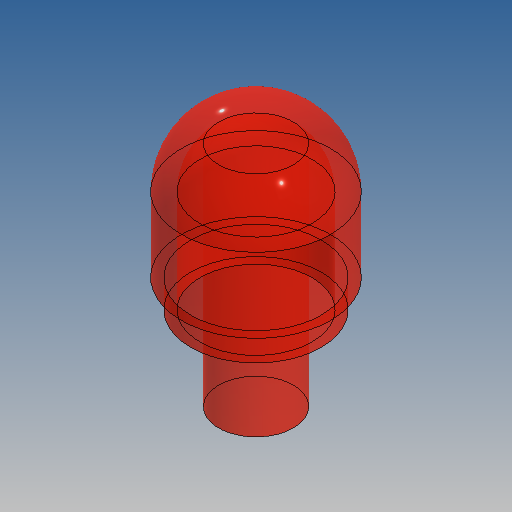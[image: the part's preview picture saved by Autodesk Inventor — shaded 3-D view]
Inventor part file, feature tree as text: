
AUTODESK INVENTOR PART (.ipt)
format: ipt  version: 2025 (Build 290162010, 162A)  size: 158,208 bytes
history: native  units: in
note: dims shown in document units (in); Inventor stores cm internally (conversion verified against a paired STEP export)
features: revolve x1, sketch x1
ambient origin geometry x8: Origin, YZ Plane, XZ Plane, XY Plane, X Axis, Y Axis, Z Axis, Center Point
bodies: Solid1 (feature_tree)
feature tree (2):
  revolve  "Revolution1"  [1 undecoded]
  sketch  "Sketch2"  dims[d0=0.1417in d1=0.252in d2=0.2205in d3=0.0472in d4=0.126in d5=0.252in d6=0.189in d7=90.0deg]
note: 1 required parameter value undecoded (feature->parameter linkage not recoverable at this tier; creation-order binding heuristic only, values carry confidence <= 0.55)
